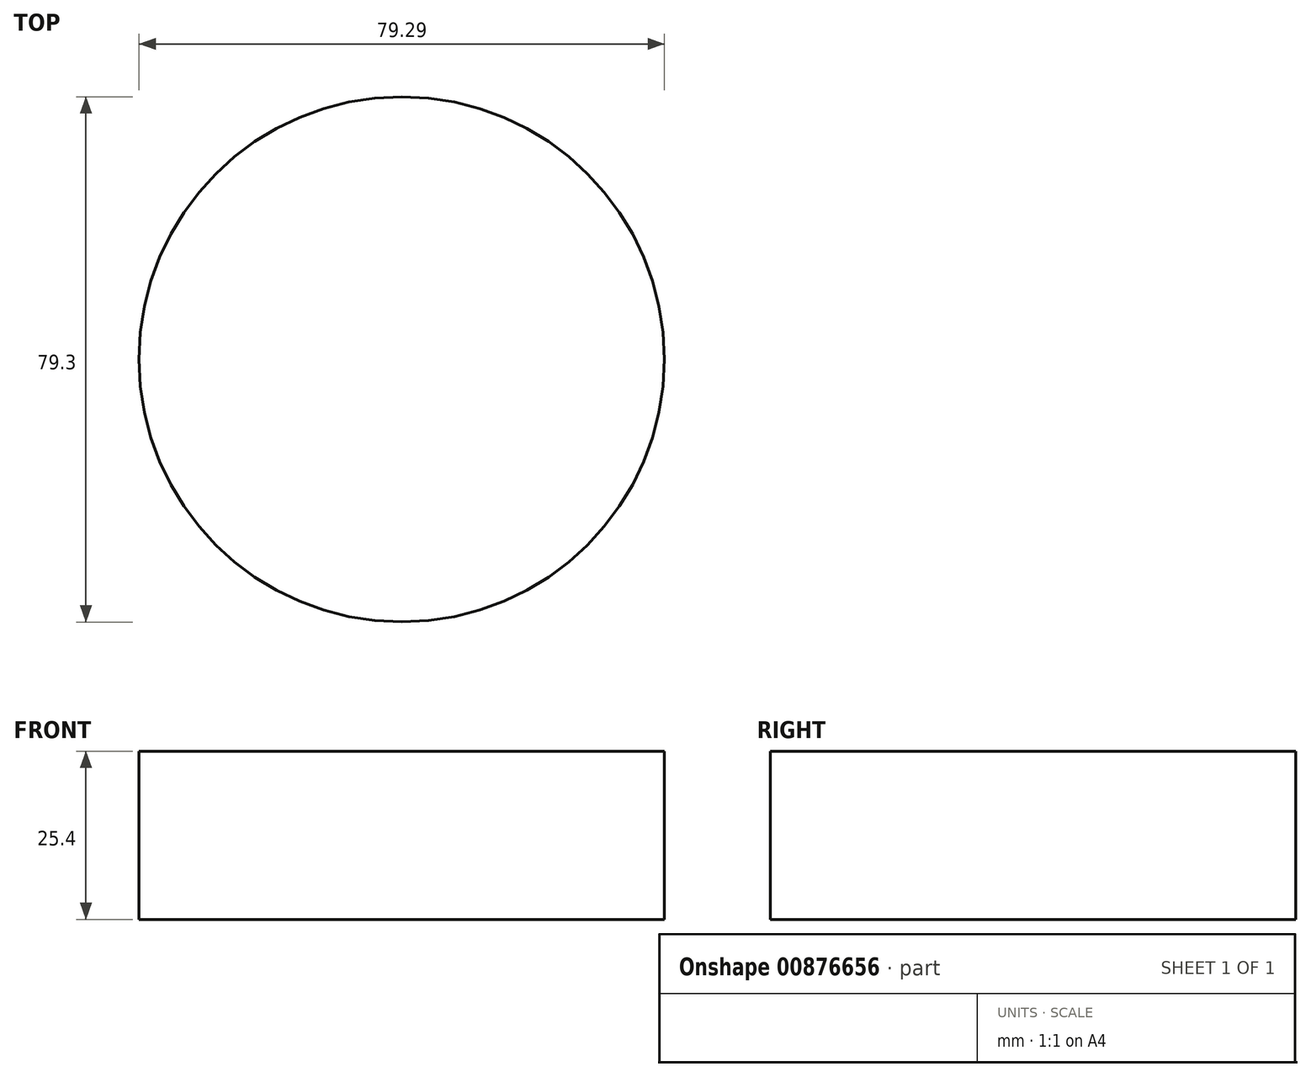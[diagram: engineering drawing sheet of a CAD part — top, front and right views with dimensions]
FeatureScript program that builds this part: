
annotation { "Feature Type Name" : "Feature", "Feature Type Description" : "" }
export const myFeature = defineFeature(function(context is Context, id is Id, definition is map)
    precondition{}
    {
        {
            var Q0;
            Q0=qCreatedBy(makeId("Top.planeOp"),FACE);
            var sketch = newSketch(context, id + "F0", { "sketchPlane" : qUnion([Q0])});
            skCircle(sketch, "E0", {"center": v(-45.36, 0) * mm, "radius": 39.65 * mm});
            skSolve(sketch);
        }
        {
            var Q0;
            Q0 = qSketchRegion(id + "F0", true);
            extrude(context, id + "F1", {"entities" : qUnion([Q0]), "depth" : 25.4 * mm, "offsetDistance" : 25.4 * mm});
        }
    });
